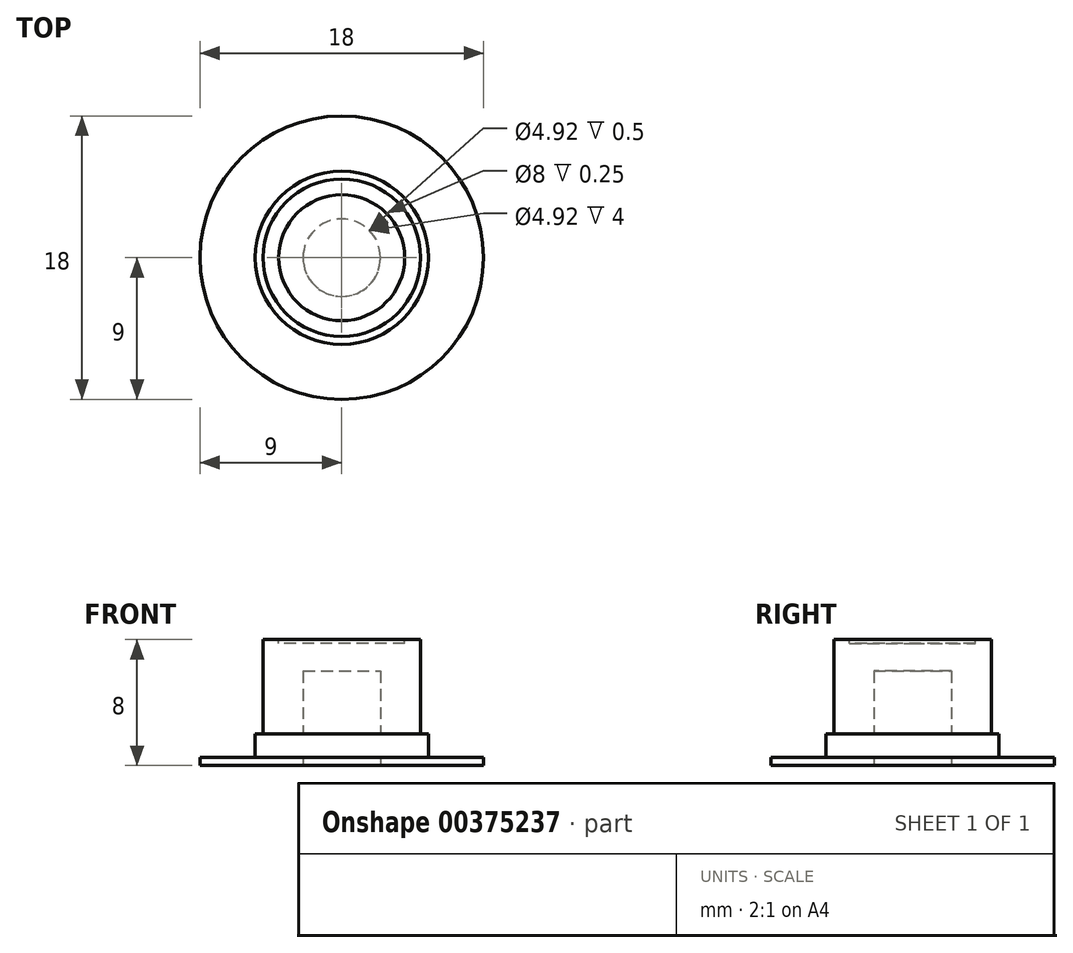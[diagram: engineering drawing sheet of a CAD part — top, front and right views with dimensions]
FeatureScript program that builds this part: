
annotation { "Feature Type Name" : "Feature", "Feature Type Description" : "" }
export const myFeature = defineFeature(function(context is Context, id is Id, definition is map)
    precondition{}
    {
        {
            var Q0;
            Q0=qCreatedBy(makeId("Top.planeOp"),FACE);
            var sketch = newSketch(context, id + "F0", { "sketchPlane" : qUnion([Q0])});
            skCircle(sketch, "E0", {"center": v(0, 0) * mm, "radius": 9 * mm});
            skSolve(sketch);
        }
        {
            var Q0;
            Q0=qSketchRegion(id+"F0",true);
            extrude(context, id + "F1", {"entities" : qUnion([Q0]), "depth" : .5 * mm});
        }
        {
            var Q0;
            Q0=makeQuery(id+"F1.opExtrude","CAP_FACE",FACE,{"disambiguationData":[OSD([sQuery(id+"F0.wireOp",EDGE,"E0")])],"isStart":false});
            var sketch = newSketch(context, id + "F2", { "sketchPlane" : qUnion([Q0])});
            skCircle(sketch, "E1", {"center": v(0, 0) * mm, "radius": 5 * mm});
            skSolve(sketch);
        }
        {
            var Q0;
            Q0=makeQuery(id+"F2.imprint","IMPRINT",FACE,{"disambiguationData":[TD([[makeQuery(id+"F2.imprint","IMPRINT",EDGE,{"derivedFrom":sQuery(id+"F2.wireOp",EDGE,"E1")}),1.0]])]});
            extrude(context, id + "F3", {"entities" : qUnion([Q0]), "operationType" : NewBodyOperationType.ADD, "depth" : 8 * mm});
        }
        {
            var Q0;
            Q0=makeQuery(id+"F1.opExtrude","CAP_FACE",FACE,{"disambiguationData":[OSD([sQuery(id+"F0.wireOp",EDGE,"E0")])],"isStart":true});
            var sketch = newSketch(context, id + "F4", { "sketchPlane" : qUnion([Q0])});
            skCircle(sketch, "E2", {"center": v(0, 0) * mm, "radius": 2.46 * mm});
            skSolve(sketch);
        }
        {
            var Q0;
            Q0=qSketchRegion(id+"F4",true);
            extrude(context, id + "F5", {"entities" : qUnion([Q0]), "operationType" : NewBodyOperationType.REMOVE, "oppositeDirection" : true, "depth" : 6 * mm});
        }
        {
            var Q0;
            Q0=makeQuery(id+"F3.opExtrude","CAP_FACE",FACE,{"disambiguationData":[OSD([sQuery(id+"F2.wireOp",EDGE,"E1")])],"isStart":false});
            var sketch = newSketch(context, id + "F6", { "sketchPlane" : qUnion([Q0])});
            skCircle(sketch, "E3", {"center": v(0, 0) * mm, "radius": 5 * mm});
            skSolve(sketch);
        }
        {
            var Q0;
            Q0=makeQuery(id+"F6.imprint","IMPRINT",FACE,{"disambiguationData":[TD([[makeQuery(id+"F6.imprint","IMPRINT",EDGE,{"derivedFrom":sQuery(id+"F6.wireOp",EDGE,"E3")}),1.0]])]});
            extrude(context, id + "F7", {"entities" : qUnion([Q0]), "operationType" : NewBodyOperationType.REMOVE, "oppositeDirection" : true, "depth" : .5 * mm});
        }
        {
            var Q0;
            Q0=makeQuery(id+"F1.opExtrude","CAP_FACE",FACE,{"disambiguationData":[OSD([sQuery(id+"F0.wireOp",EDGE,"E0")])],"isStart":false});
            var sketch = newSketch(context, id + "F8", { "sketchPlane" : qUnion([Q0])});
            skCircle(sketch, "E4", {"center": v(0, 0) * mm, "radius": 5.5 * mm});
            skSolve(sketch);
        }
        {
            var Q0;
            Q0=qSketchRegion(id+"F8",true);
            extrude(context, id + "F9", {"entities" : qUnion([Q0]), "operationType" : NewBodyOperationType.ADD, "depth" : 1.5 * mm});
        }
        {
            var Q0;
            Q0=makeQuery(id+"F7.boolean.opBoolean","COPY",FACE,{"derivedFrom":makeQuery(id+"F7.opExtrude","CAP_FACE",FACE,{"disambiguationData":[OSD([sQuery(id+"F6.wireOp",EDGE,"E3")])],"isStart":false})});
            var sketch = newSketch(context, id + "F10", { "sketchPlane" : qUnion([Q0])});
            skCircle(sketch, "E5", {"center": v(0, 0) * mm, "radius": 4 * mm});
            skSolve(sketch);
        }
        {
            var Q0;
            Q0=makeQuery(id+"F10.imprint","IMPRINT",FACE,{"disambiguationData":[TD([[makeQuery(id+"F10.imprint","IMPRINT",EDGE,{"derivedFrom":sQuery(id+"F10.wireOp",EDGE,"E5")}),1.0]])]});
            extrude(context, id + "F11", {"entities" : qUnion([Q0]), "operationType" : NewBodyOperationType.REMOVE, "oppositeDirection" : true, "depth" : .25 * mm});
        }
    });
